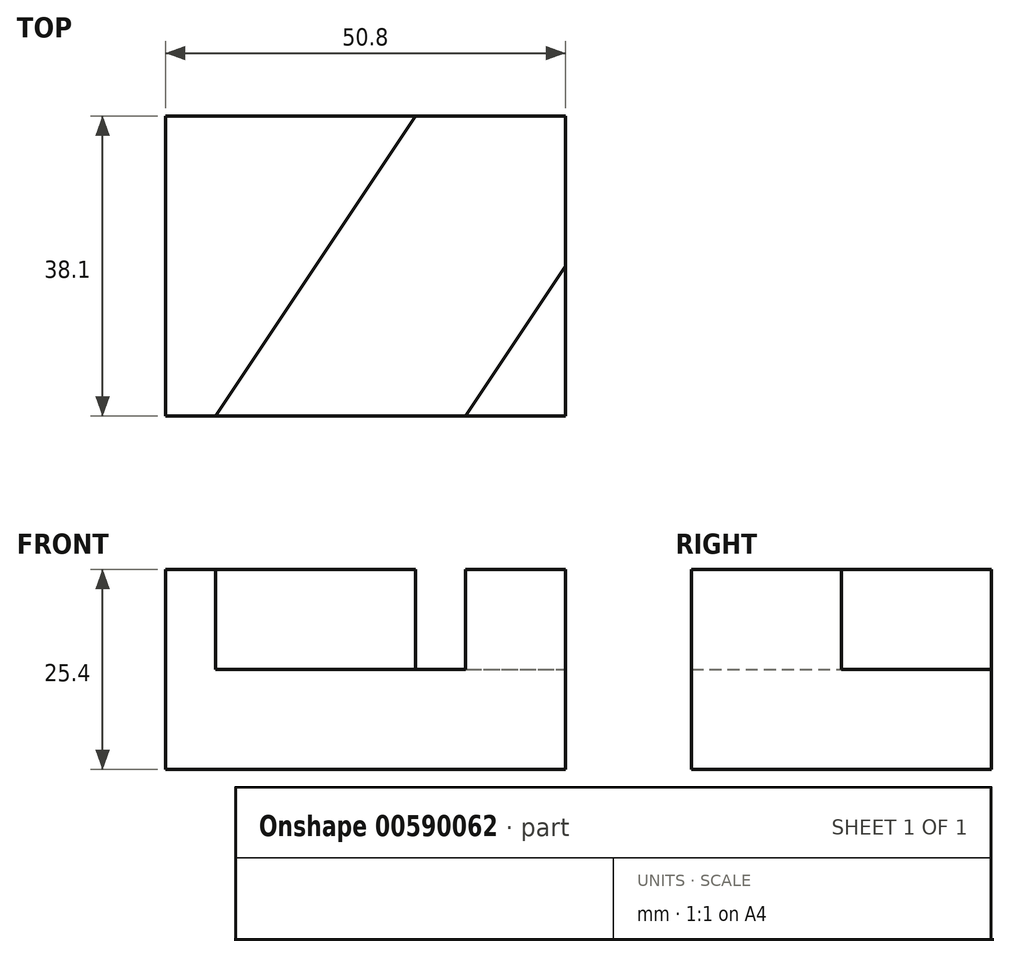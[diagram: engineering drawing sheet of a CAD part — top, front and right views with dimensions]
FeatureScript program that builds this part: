
annotation { "Feature Type Name" : "Feature", "Feature Type Description" : "" }
export const myFeature = defineFeature(function(context is Context, id is Id, definition is map)
    precondition{}
    {
        {
            var Q0;
            Q0=qCreatedBy(makeId("Front.planeOp"),FACE);
            var sketch = newSketch(context, id + "F0", { "sketchPlane" : qUnion([Q0])});
            skLineSegment(sketch, "E0", {"start": v(-62.32, 49.59) * mm, "end": v(-62.32, 24.19) * mm});
            skLineSegment(sketch, "E1", {"start": v(-62.32, 24.19) * mm, "end": v(-11.52, 24.19) * mm});
            skLineSegment(sketch, "E2", {"start": v(-62.32, 49.59) * mm, "end": v(-11.52, 49.59) * mm});
            skLineSegment(sketch, "E3", {"start": v(-11.52, 49.59) * mm, "end": v(-11.52, 24.19) * mm});
            skSolve(sketch);
        }
        {
            var Q0;
            Q0 = qSketchRegion(id + "F0", true);
            extrude(context, id + "F1", {"entities" : qUnion([Q0]), "depth" : 38.1 * mm, "offsetDistance" : 25.4 * mm});
        }
        {
            var Q0;
            Q0=makeQuery(id+"F1.opExtrude","SWEPT_FACE",FACE,{"disambiguationData":[OSD([sQuery(id+"F0.wireOp",EDGE,"E2")])]});
            var sketch = newSketch(context, id + "F2", { "sketchPlane" : qUnion([Q0])});
            skLineSegment(sketch, "E4", {"start": v(-55.97, -38.1) * mm, "end": v(-30.57, 0) * mm});
            skLineSegment(sketch, "E5", {"start": v(-24.22, -38.1) * mm, "end": v(-11.52, -19.05) * mm});
            skSolve(sketch);
        }
        {
            var Q0;
            Q0 = qSketchRegion(id + "F2", true);
            var Q1;
            {var subQ5=sQuery(id+"F2.wireOp",EDGE,"E4");Q1=makeQuery(id+"F2.imprint","IMPRINT",FACE,{"disambiguationData":[TD([[makeQuery(id+"F2.imprint","IMPRINT",EDGE,{"derivedFrom":subQ5}),-1.0]])]});}
            extrude(context, id + "F3", {"entities" : qUnion([Q0, Q1]), "operationType" : NewBodyOperationType.REMOVE, "oppositeDirection" : true, "depth" : 12.7 * mm, "offsetDistance" : 25.4 * mm});
        }
    });
